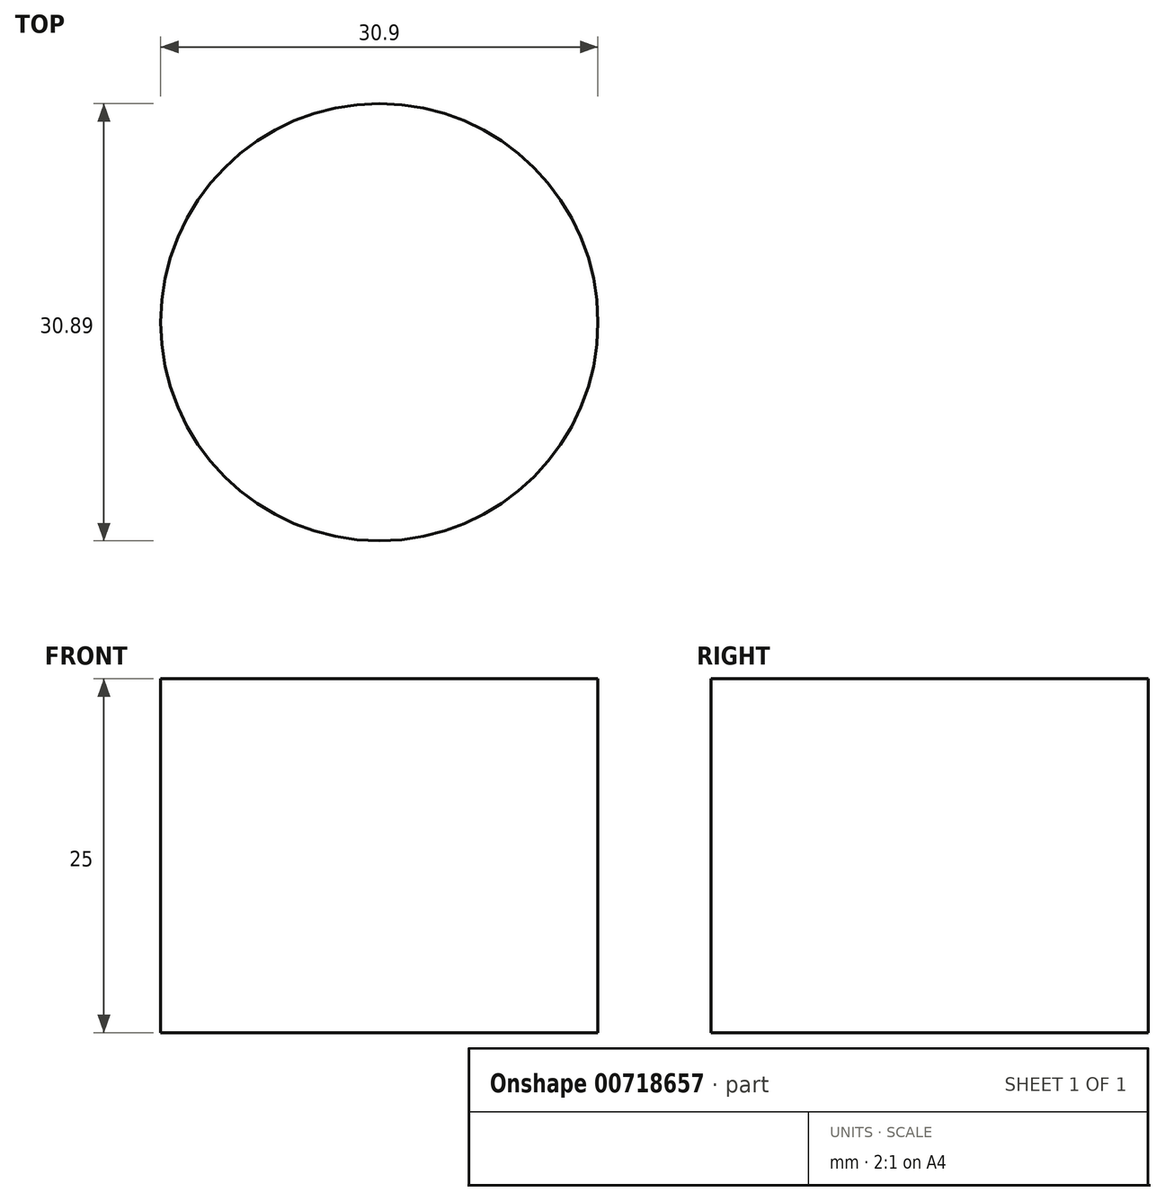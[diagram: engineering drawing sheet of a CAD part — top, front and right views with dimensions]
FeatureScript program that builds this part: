
annotation { "Feature Type Name" : "Feature", "Feature Type Description" : "" }
export const myFeature = defineFeature(function(context is Context, id is Id, definition is map)
    precondition{}
    {
        {
            var Q0;
            Q0=qCreatedBy(makeId("Top.planeOp"),FACE);
            var sketch = newSketch(context, id + "F0", { "sketchPlane" : qUnion([Q0])});
            skCircle(sketch, "E0", {"center": v(66.61, 41.68) * mm, "radius": 15.45 * mm});
            skSolve(sketch);
        }
        {
            var Q0;
            Q0 = qSketchRegion(id + "F0", true);
            extrude(context, id + "F1", {"entities" : qUnion([Q0]), "depth" : 25 * mm, "offsetDistance" : 25 * mm});
        }
    });
